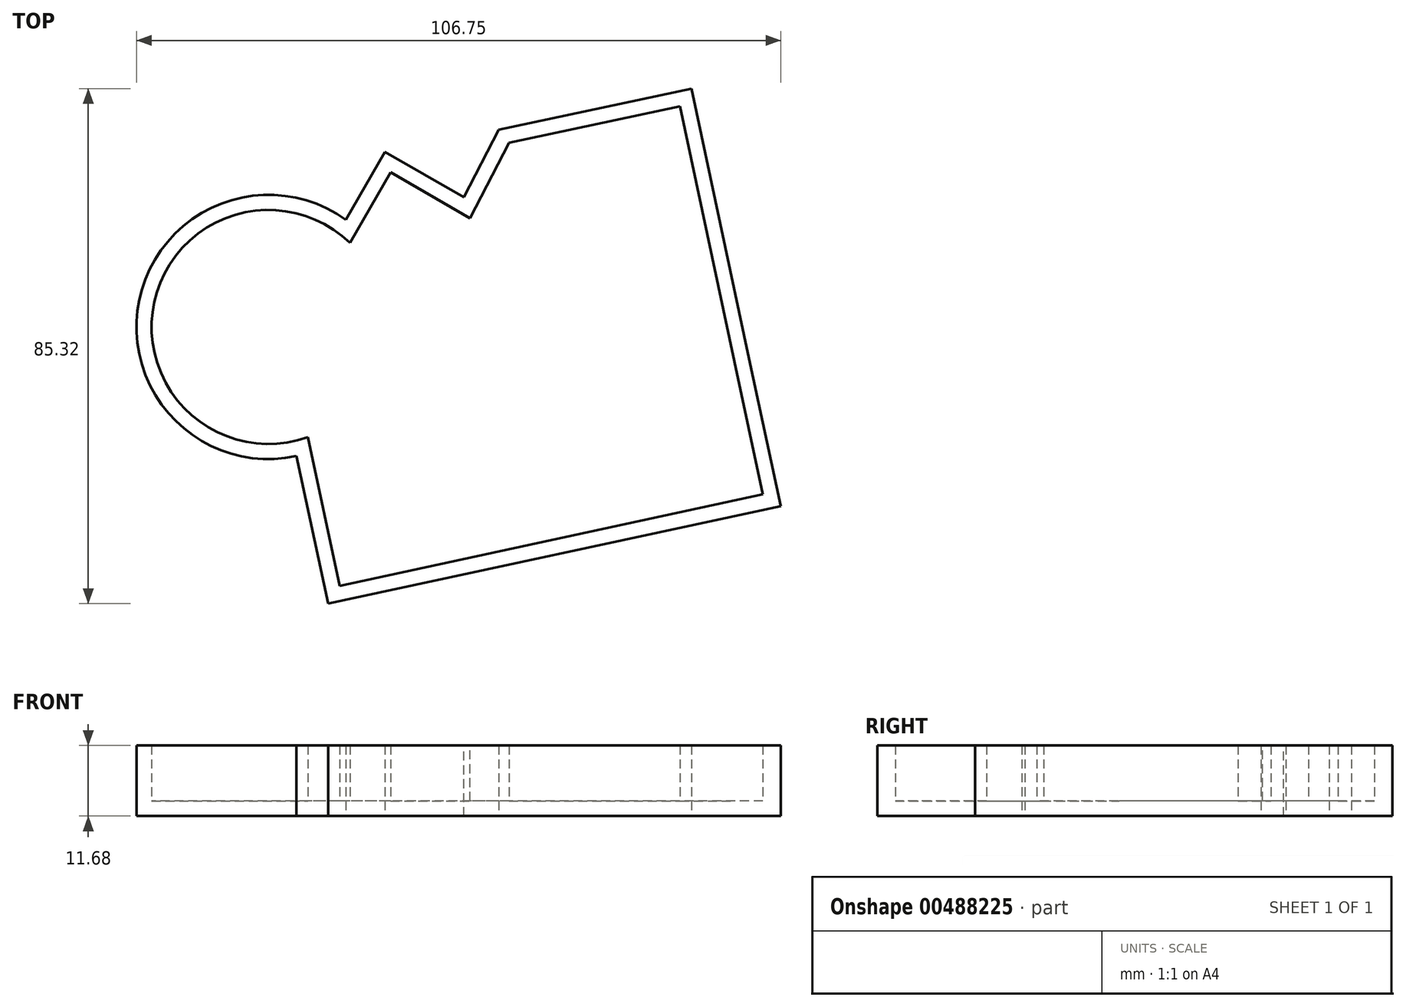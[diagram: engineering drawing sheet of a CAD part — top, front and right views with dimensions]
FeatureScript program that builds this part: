
annotation { "Feature Type Name" : "Feature", "Feature Type Description" : "" }
export const myFeature = defineFeature(function(context is Context, id is Id, definition is map)
    precondition{}
    {
        {
            var Q0;
            Q0=qCreatedBy(makeId("Top.planeOp"),FACE);
            var sketch = newSketch(context, id + "F0", { "sketchPlane" : qUnion([Q0])});
            skLineSegment(sketch, "E0", {"start": v(-114.95, 39.32) * mm, "end": v(-101.04, 31.31) * mm});
            skLineSegment(sketch, "E1", {"start": v(-89.3, 54.09) * mm, "end": v(-101.04, 31.31) * mm});
            skLineSegment(sketch, "E2", {"start": v(-89.3, 54.09) * mm, "end": v(-57.35, 60.88) * mm});
            skLineSegment(sketch, "E3", {"start": v(-57.35, 60.88) * mm, "end": v(-47.85, 16.18) * mm});
            skLineSegment(sketch, "E4", {"start": v(-47.85, 16.18) * mm, "end": v(-122.83, 0) * mm});
            skArc(sketch, "E5", {"start": v(-122.83, 0) * mm, "mid": v(-148.87, 25.88) * mm, "end": v(-114.64, 39.14) * mm});
            skSolve(sketch);
        }
        {
            var Q0;
            {var subQ0=sQuery(id+"F0.wireOp",EDGE,"E1");Q0=makeQuery(id+"F0.imprint","IMPRINT",FACE,{"disambiguationData":[TD([[makeQuery(id+"F0.imprint","IMPRINT",EDGE,{"derivedFrom":subQ0}),1.0]])]});}
            extrude(context, id + "F1", {"entities" : qUnion([Q0]), "depth" : 11.68 * mm});
        }
        {
            var Q0;
            Q0=makeQuery(id+"F1.opExtrude","SWEPT_FACE",FACE,{"disambiguationData":[OSD([sQuery(id+"F0.wireOp",EDGE,"E4")])]});
            extrude(context, id + "F2", {"entities" : qUnion([Q0]), "operationType" : NewBodyOperationType.ADD, "depth" : 25 * mm});
        }
        {
            var Q0;
            Q0=makeQuery(id+"F1.opExtrude","SWEPT_FACE",FACE,{"disambiguationData":[OSD([sQuery(id+"F0.wireOp",EDGE,"E0")])]});
            extrude(context, id + "F3", {"entities" : qUnion([Q0]), "operationType" : NewBodyOperationType.ADD, "depth" : 13 * mm});
        }
        {
            var Q0;
            {var subQ0=sQuery(id+"F0.wireOp",EDGE,"E0");var subQ1=sQuery(id+"F0.wireOp",EDGE,"E4");Q0=makeQuery(id+"F3.boolean.opBoolean","MERGE",FACE,{"derivedFrom":[makeQuery(id+"F2.boolean.opBoolean","MERGE",FACE,{"derivedFrom":[makeQuery(id+"F1.opExtrude","CAP_FACE",FACE,{"disambiguationData":[OSD([subQ0,sQuery(id+"F0.wireOp",EDGE,"E1"),sQuery(id+"F0.wireOp",EDGE,"E2"),sQuery(id+"F0.wireOp",EDGE,"E3"),subQ1,sQuery(id+"F0.wireOp",EDGE,"E5")])],"isStart":false}),makeQuery(id+"F2.opExtrude","SWEPT_FACE",FACE,{"disambiguationData":[OSD([subQ1]),TDD([makeQuery(id+"F1.opExtrude","CAP_EDGE",EDGE,{"disambiguationData":[OSD([subQ1])],"isStart":false})])]})]}),makeQuery(id+"F3.opExtrude","SWEPT_FACE",FACE,{"disambiguationData":[OSD([subQ0]),TDD([makeQuery(id+"F1.opExtrude","CAP_EDGE",EDGE,{"disambiguationData":[OSD([subQ0])],"isStart":false})])]})]});}
            shell(context, id + "F4", {"entities" : qUnion([Q0]), "thickness" : 2.5 * mm});
        }
    });
